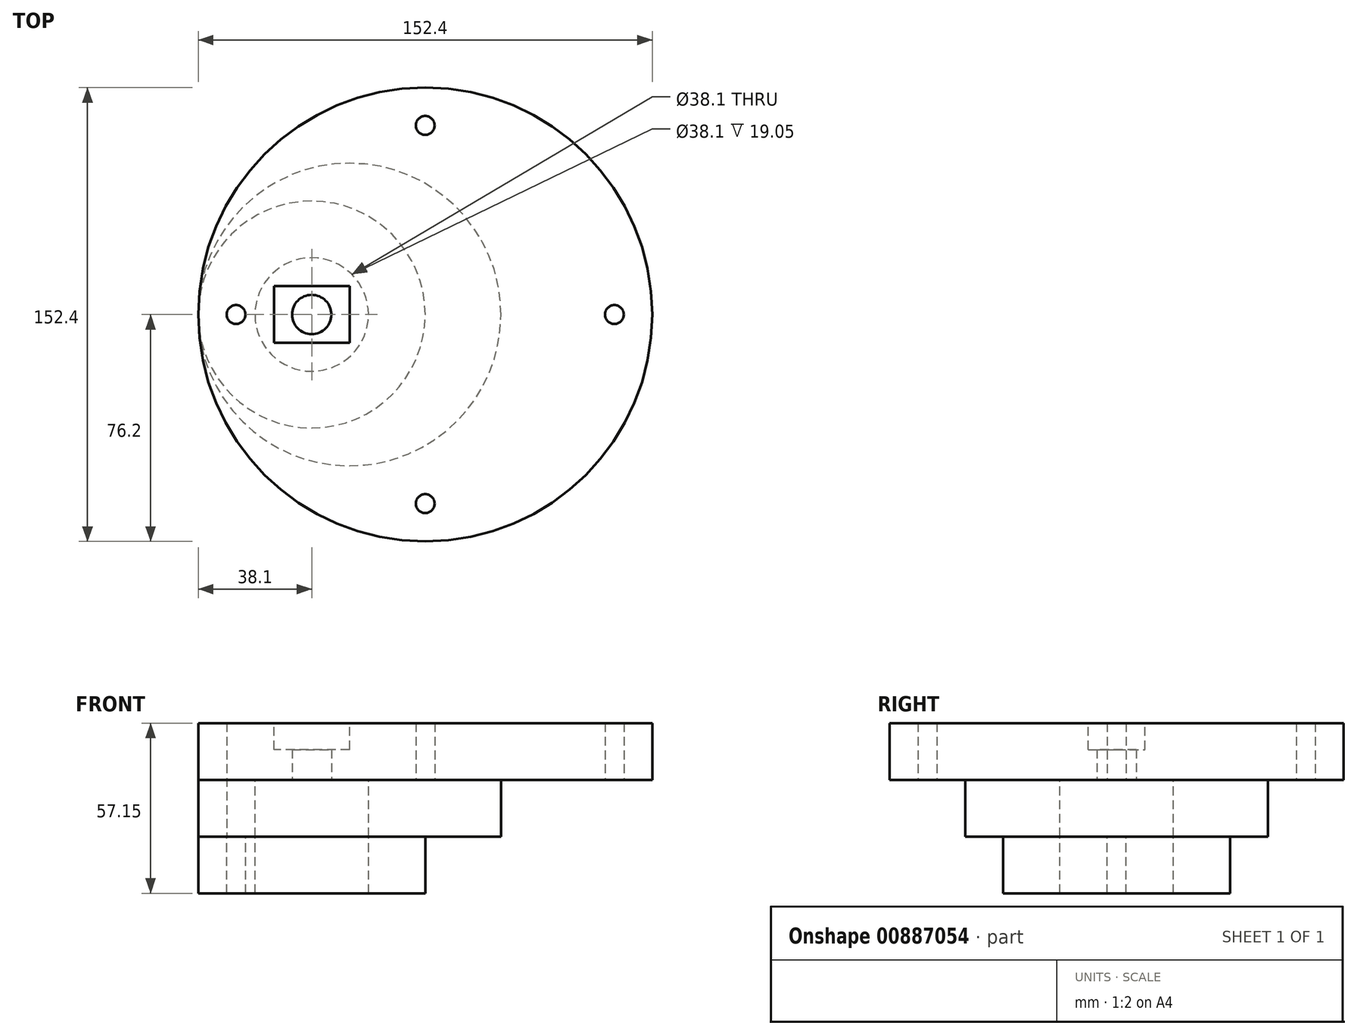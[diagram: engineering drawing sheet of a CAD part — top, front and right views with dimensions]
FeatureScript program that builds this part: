
annotation { "Feature Type Name" : "Feature", "Feature Type Description" : "" }
export const myFeature = defineFeature(function(context is Context, id is Id, definition is map)
    precondition{}
    {
        {
            var Q0;
            Q0=qCreatedBy(makeId("Top.planeOp"),FACE);
            var sketch = newSketch(context, id + "F0", { "sketchPlane" : qUnion([Q0])});
            skCircle(sketch, "E0", {"center": v(0, 0) * mm, "radius": 76.2 * mm});
            skSolve(sketch);
        }
        {
            var Q0;
            Q0=makeQuery(id+"F0.imprint","IMPRINT",FACE,{"disambiguationData":[TD([[makeQuery(id+"F0.imprint","IMPRINT",EDGE,{"derivedFrom":sQuery(id+"F0.wireOp",EDGE,"E0")}),1.0]])]});
            extrude(context, id + "F1", {"entities" : qUnion([Q0]), "depth" : 19.05 * mm, "offsetDistance" : 25.4 * mm});
        }
        {
            var Q0;
            Q0=makeQuery(id+"F1.opExtrude","CAP_FACE",FACE,{"disambiguationData":[OSD([sQuery(id+"F0.wireOp",EDGE,"E0")])],"isStart":false});
            var sketch = newSketch(context, id + "F2", { "sketchPlane" : qUnion([Q0])});
            skLineSegment(sketch, "E1.bottom", {"start": v(-25.4, -9.52) * mm, "end": v(-50.8, -9.52) * mm});
            skLineSegment(sketch, "E1.top", {"start": v(-25.4, 9.53) * mm, "end": v(-50.8, 9.53) * mm});
            skLineSegment(sketch, "E1.left", {"start": v(-25.4, -9.52) * mm, "end": v(-25.4, 9.53) * mm});
            skLineSegment(sketch, "E1.right", {"start": v(-50.8, -9.52) * mm, "end": v(-50.8, 9.53) * mm});
            skPoint(sketch, "E2", {"position": v(-38.1, 0) * mm});
            skSolve(sketch);
        }
        {
            var Q0;
            Q0=makeQuery(id+"F2.imprint","IMPRINT",FACE,{"disambiguationData":[TD([[makeQuery(id+"F2.imprint","IMPRINT",EDGE,{"derivedFrom":sQuery(id+"F2.wireOp",EDGE,"E1.bottom")}),-1.0]])]});
            extrude(context, id + "F3", {"entities" : qUnion([Q0]), "operationType" : NewBodyOperationType.REMOVE, "oppositeDirection" : true, "depth" : 8.9 * mm, "offsetDistance" : 25.4 * mm});
        }
        {
            var Q0;
            Q0=makeQuery(id+"F1.opExtrude","CAP_FACE",FACE,{"disambiguationData":[OSD([sQuery(id+"F0.wireOp",EDGE,"E0")])],"isStart":true});
            var sketch = newSketch(context, id + "F4", { "sketchPlane" : qUnion([Q0])});
            skCircle(sketch, "E3", {"center": v(-38.1, 0) * mm, "radius": 6.6 * mm});
            skSolve(sketch);
        }
        {
            var Q0;
            Q0=qSketchRegion(id+"F4",true);
            extrude(context, id + "F5", {"entities" : qUnion([Q0]), "operationType" : NewBodyOperationType.REMOVE, "oppositeDirection" : true, "depth" : 10.16 * mm, "offsetDistance" : 25.4 * mm});
        }
        {
            var Q0;
            Q0=makeQuery(id+"F1.opExtrude","CAP_FACE",FACE,{"disambiguationData":[OSD([sQuery(id+"F0.wireOp",EDGE,"E0")])],"isStart":true});
            var sketch = newSketch(context, id + "F6", { "sketchPlane" : qUnion([Q0])});
            skCircle(sketch, "E4", {"center": v(0, 0) * mm, "radius": 63.5 * mm, "construction": true});
            skLineSegment(sketch, "E5", {"start": v(63.5, 0) * mm, "end": v(-63.5, 0) * mm, "construction": true});
            skLineSegment(sketch, "E6", {"start": v(0, 63.5) * mm, "end": v(0, -63.5) * mm, "construction": true});
            skCircle(sketch, "E7", {"center": v(0, 63.5) * mm, "radius": 3.18 * mm});
            skCircle(sketch, "E8", {"center": v(-63.5, 0) * mm, "radius": 3.18 * mm});
            skCircle(sketch, "E9", {"center": v(0, -63.5) * mm, "radius": 3.18 * mm});
            skCircle(sketch, "E10", {"center": v(63.5, 0) * mm, "radius": 3.18 * mm});
            skSolve(sketch);
        }
        {
            var Q0;
            Q0=makeQuery(id+"F6.imprint","IMPRINT",FACE,{"disambiguationData":[TD([[makeQuery(id+"F6.imprint","IMPRINT",EDGE,{"derivedFrom":sQuery(id+"F6.wireOp",EDGE,"E7")}),1.0]])]});
            var Q1;
            Q1=makeQuery(id+"F6.imprint","IMPRINT",FACE,{"disambiguationData":[TD([[makeQuery(id+"F6.imprint","IMPRINT",EDGE,{"derivedFrom":sQuery(id+"F6.wireOp",EDGE,"E10")}),1.0]])]});
            var Q2;
            Q2=makeQuery(id+"F6.imprint","IMPRINT",FACE,{"disambiguationData":[TD([[makeQuery(id+"F6.imprint","IMPRINT",EDGE,{"derivedFrom":sQuery(id+"F6.wireOp",EDGE,"E9")}),1.0]])]});
            var Q3;
            Q3=makeQuery(id+"F6.imprint","IMPRINT",FACE,{"disambiguationData":[TD([[makeQuery(id+"F6.imprint","IMPRINT",EDGE,{"derivedFrom":sQuery(id+"F6.wireOp",EDGE,"E8")}),1.0]])]});
            extrude(context, id + "F7", {"entities" : qUnion([Q0, Q1, Q2, Q3]), "operationType" : NewBodyOperationType.REMOVE, "oppositeDirection" : true, "depth" : 19.05 * mm, "offsetDistance" : 25.4 * mm});
        }
        {
            var Q0;
            Q0=makeQuery(id+"F1.opExtrude","CAP_FACE",FACE,{"disambiguationData":[OSD([sQuery(id+"F0.wireOp",EDGE,"E0")])],"isStart":true});
            var sketch = newSketch(context, id + "F8", { "sketchPlane" : qUnion([Q0])});
            skCircle(sketch, "E11", {"center": v(-25.4, 0) * mm, "radius": 50.8 * mm});
            skCircle(sketch, "E12", {"center": v(-38.1, 0) * mm, "radius": 19.05 * mm});
            skSolve(sketch);
        }
        {
            var Q0;
            Q0=makeQuery(id+"F8.imprint","IMPRINT",FACE,{"disambiguationData":[TD([[makeQuery(id+"F8.imprint","IMPRINT",EDGE,{"derivedFrom":sQuery(id+"F8.wireOp",EDGE,"E11")}),1.0]])]});
            extrude(context, id + "F9", {"entities" : qUnion([Q0]), "operationType" : NewBodyOperationType.ADD, "depth" : 19.05 * mm, "offsetDistance" : 25.4 * mm});
        }
        {
            var Q0;
            Q0=makeQuery(id+"F9.opExtrude","CAP_FACE",FACE,{"disambiguationData":[OSD([sQuery(id+"F6.wireOp",EDGE,"E8"),sQuery(id+"F8.wireOp",EDGE,"E11"),sQuery(id+"F8.wireOp",EDGE,"E12")])],"isStart":false});
            var sketch = newSketch(context, id + "F10", { "sketchPlane" : qUnion([Q0])});
            skCircle(sketch, "E13", {"center": v(-38.1, 0) * mm, "radius": 38.1 * mm});
            skCircle(sketch, "E14", {"center": v(-38.1, 0) * mm, "radius": 19.05 * mm});
            skSolve(sketch);
        }
        {
            var Q0;
            Q0=makeQuery(id+"F10.imprint","IMPRINT",FACE,{"disambiguationData":[TD([[makeQuery(id+"F10.imprint","IMPRINT",EDGE,{"derivedFrom":sQuery(id+"F10.wireOp",EDGE,"E13")}),1.0]])]});
            extrude(context, id + "F11", {"entities" : qUnion([Q0]), "depth" : 19.05 * mm, "offsetDistance" : 25.4 * mm});
        }
    });
